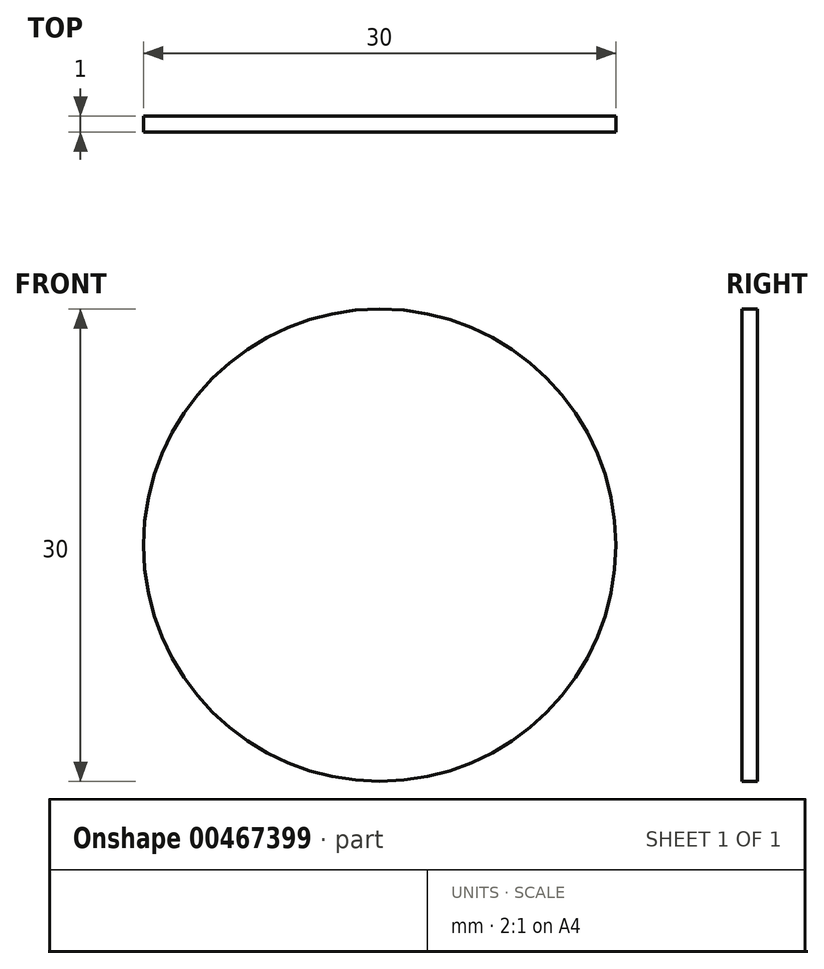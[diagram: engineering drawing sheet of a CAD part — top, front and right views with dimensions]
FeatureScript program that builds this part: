
annotation { "Feature Type Name" : "Feature", "Feature Type Description" : "" }
export const myFeature = defineFeature(function(context is Context, id is Id, definition is map)
    precondition{}
    {
        {
            var Q0;
            Q0=qCreatedBy(makeId("Front.planeOp"),FACE);
            var sketch = newSketch(context, id + "F0", { "sketchPlane" : qUnion([Q0])});
            skCircle(sketch, "E0", {"center": v(0, 0) * mm, "radius": 15 * mm});
            skSolve(sketch);
        }
        {
            var Q0;
            Q0=makeQuery(id+"F0.imprint","IMPRINT",FACE,{"disambiguationData":[TD([[makeQuery(id+"F0.imprint","IMPRINT",EDGE,{"derivedFrom":sQuery(id+"F0.wireOp",EDGE,"E0")}),1.0]])]});
            extrude(context, id + "F1", {"entities" : qUnion([Q0]), "depth" : 1 * mm, "offsetDistance" : 25 * mm});
        }
    });
